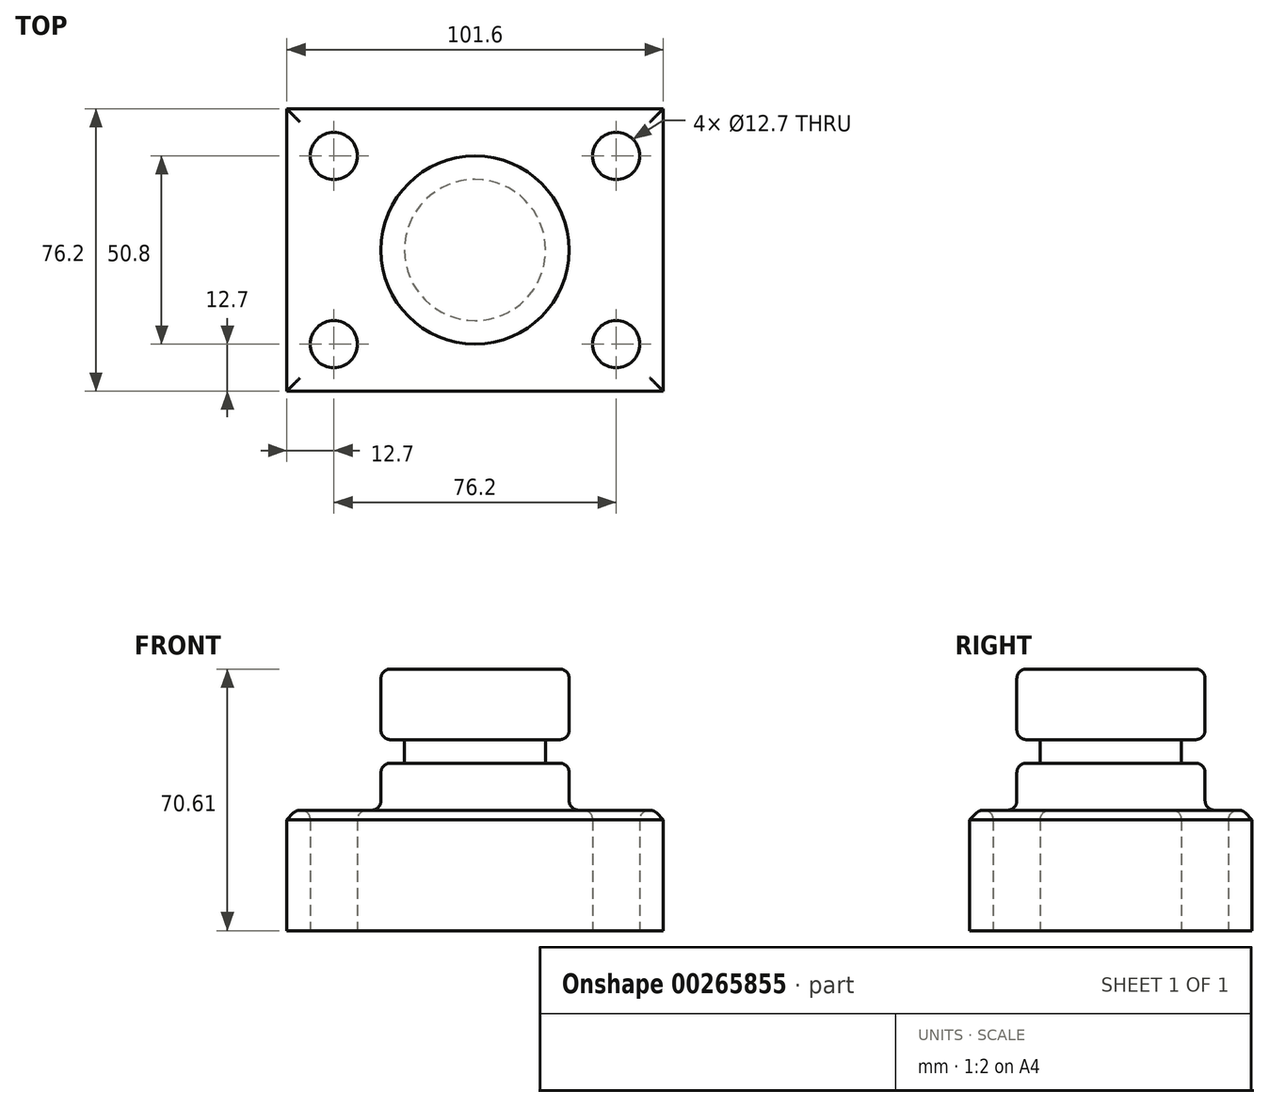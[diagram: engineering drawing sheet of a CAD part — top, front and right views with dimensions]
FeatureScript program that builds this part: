
annotation { "Feature Type Name" : "Feature", "Feature Type Description" : "" }
export const myFeature = defineFeature(function(context is Context, id is Id, definition is map)
    precondition{}
    {
        {
            var Q0;
            Q0=qCreatedBy(makeId("Top.planeOp"),FACE);
            var sketch = newSketch(context, id + "F0", { "sketchPlane" : qUnion([Q0])});
            skLineSegment(sketch, "E0.bottom", {"start": v(50.8, 38.1) * mm, "end": v(-50.8, 38.1) * mm});
            skLineSegment(sketch, "E0.top", {"start": v(50.8, -38.1) * mm, "end": v(-50.8, -38.1) * mm});
            skLineSegment(sketch, "E0.left", {"start": v(50.8, 38.1) * mm, "end": v(50.8, -38.1) * mm});
            skLineSegment(sketch, "E0.right", {"start": v(-50.8, 38.1) * mm, "end": v(-50.8, -38.1) * mm});
            skPoint(sketch, "E0.middle", {"position": v(0, 0) * mm});
            skSolve(sketch);
        }
        {
            var Q0;
            Q0 = qSketchRegion(id + "F0", true);
            extrude(context, id + "F1", {"entities" : qUnion([Q0]), "depth" : 32.5 * mm});
        }
        {
            var Q0;
            Q0=qCreatedBy(makeId("Top.planeOp"),FACE);
            var sketch = newSketch(context, id + "F2", { "sketchPlane" : qUnion([Q0])});
            skCircle(sketch, "E1", {"center": v(-38.1, -25.4) * mm, "radius": 6.35 * mm});
            skCircle(sketch, "E2", {"center": v(38.1, -25.4) * mm, "radius": 6.35 * mm});
            skCircle(sketch, "E3", {"center": v(-38.1, 25.4) * mm, "radius": 6.35 * mm});
            skCircle(sketch, "E4", {"center": v(38.1, 25.4) * mm, "radius": 6.35 * mm});
            skSolve(sketch);
        }
        {
            var Q0;
            Q0=makeQuery(id+"F2.imprint","IMPRINT",FACE,{"disambiguationData":[TD([[makeQuery(id+"F2.imprint","IMPRINT",EDGE,{"derivedFrom":sQuery(id+"F2.wireOp",EDGE,"E1")}),1.0]])]});
            extrude(context, id + "F3", {"entities" : qUnion([Q0]), "operationType" : NewBodyOperationType.REMOVE, "depth" : 32.77 * mm});
        }
        {
            var Q0;
            Q0 = qSketchRegion(id + "F2", true);
            extrude(context, id + "F4", {"entities" : qUnion([Q0]), "operationType" : NewBodyOperationType.REMOVE, "depth" : 32.77 * mm});
        }
        {
            var Q0;
            Q0=qCreatedBy(makeId("Front.planeOp"),FACE);
            var sketch = newSketch(context, id + "F5", { "sketchPlane" : qUnion([Q0])});
            skLineSegment(sketch, "E5.bottom", {"start": v(0, 70.61) * mm, "end": v(-25.4, 70.61) * mm});
            skLineSegment(sketch, "E5.top", {"start": v(0, 32.51) * mm, "end": v(-25.4, 32.51) * mm});
            skLineSegment(sketch, "E5.left", {"start": v(0, 70.61) * mm, "end": v(0, 32.51) * mm});
            skLineSegment(sketch, "E5.right", {"start": v(-25.4, 70.61) * mm, "end": v(-25.4, 32.51) * mm});
            skSolve(sketch);
        }
        {
            var Q0;
            Q0 = qSketchRegion(id + "F5", true);
            var Q1;
            Q1=sQuery(id+"F5.wireOp",EDGE,"E5.left");
            revolve(context, id + "F6", {"operationType" : NewBodyOperationType.ADD, "entities" : qUnion([Q0]), "axis" : qUnion([Q1]), "revolveType" : RevolveType.FULL});
        }
        {
            var Q0;
            Q0=qCreatedBy(makeId("Right.planeOp"),FACE);
            var sketch = newSketch(context, id + "F7", { "sketchPlane" : qUnion([Q0])});
            skLineSegment(sketch, "E6.bottom", {"start": v(-19.05, 51.56) * mm, "end": v(-34.38, 51.56) * mm});
            skLineSegment(sketch, "E6.top", {"start": v(-19.05, 45.21) * mm, "end": v(-34.38, 45.21) * mm});
            skLineSegment(sketch, "E6.left", {"start": v(-19.05, 51.56) * mm, "end": v(-19.05, 45.21) * mm});
            skLineSegment(sketch, "E6.right", {"start": v(-34.38, 51.56) * mm, "end": v(-34.38, 45.21) * mm});
            skSolve(sketch);
        }
        {
            var Q0;
            Q0=makeQuery(id+"F7.imprint","IMPRINT",FACE,{"disambiguationData":[TD([[makeQuery(id+"F7.imprint","IMPRINT",EDGE,{"derivedFrom":sQuery(id+"F7.wireOp",EDGE,"E6.bottom")}),1.0]])]});
            var Q1;
            Q1=makeQuery(id+"F6.opRevolve","SWEPT_FACE",FACE,{"disambiguationData":[OSD([sQuery(id+"F5.wireOp",EDGE,"E5.right")])]});
            revolve(context, id + "F8", {"operationType" : NewBodyOperationType.REMOVE, "entities" : qUnion([Q0]), "axis" : qUnion([Q1]), "revolveType" : RevolveType.FULL, "oppositeDirection" : true});
        }
        {
            var Q0;
            Q0=makeQuery(id+"F1.opExtrude","CAP_EDGE",EDGE,{"disambiguationData":[OSD([sQuery(id+"F0.wireOp",EDGE,"E0.left")])],"isStart":false});
            var Q1;
            Q1=makeQuery(id+"F1.opExtrude","CAP_EDGE",EDGE,{"disambiguationData":[OSD([sQuery(id+"F0.wireOp",EDGE,"E0.bottom")])],"isStart":false});
            var Q2;
            Q2=makeQuery(id+"F1.opExtrude","CAP_EDGE",EDGE,{"disambiguationData":[OSD([sQuery(id+"F0.wireOp",EDGE,"E0.right")])],"isStart":false});
            var Q3;
            Q3=makeQuery(id+"F1.opExtrude","CAP_EDGE",EDGE,{"disambiguationData":[OSD([sQuery(id+"F0.wireOp",EDGE,"E0.top")])],"isStart":false});
            chamfer(context, id + "F9", {"entities" : qUnion([Q0, Q1, Q2, Q3]), "width" : 2.54 * mm, "tangentPropagation" : true});
        }
        {
            var Q0;
            Q0=makeQuery(id+"F6.opRevolve","SWEPT_EDGE",EDGE,{"disambiguationData":[OSD([sQuery(id+"F5.wireOp",EDGE,"E5.bottom"),sQuery(id+"F5.wireOp",EDGE,"E5.right")])]});
            var Q1;
            Q1=makeQuery(id+"F8.boolean.opBoolean","INTERSECT",EDGE,{"derivedFrom":[makeQuery(id+"F6.opRevolve","SWEPT_FACE",FACE,{"disambiguationData":[OSD([sQuery(id+"F5.wireOp",EDGE,"E5.right")])]}),makeQuery(id+"F8.opRevolve","SWEPT_FACE",FACE,{"disambiguationData":[OSD([sQuery(id+"F7.wireOp",EDGE,"E6.top")])]})]});
            var Q2;
            Q2=makeQuery(id+"F8.boolean.opBoolean","INTERSECT",EDGE,{"derivedFrom":[makeQuery(id+"F6.opRevolve","SWEPT_FACE",FACE,{"disambiguationData":[OSD([sQuery(id+"F5.wireOp",EDGE,"E5.right")])]}),makeQuery(id+"F8.opRevolve","SWEPT_FACE",FACE,{"disambiguationData":[OSD([sQuery(id+"F7.wireOp",EDGE,"E6.bottom")])]})]});
            var Q3;
            Q3=makeQuery(id+"F4.boolean.opBoolean","INTERSECT",EDGE,{"derivedFrom":[makeQuery(id+"F1.opExtrude","CAP_FACE",FACE,{"disambiguationData":[OSD([sQuery(id+"F0.wireOp",EDGE,"E0.bottom"),sQuery(id+"F0.wireOp",EDGE,"E0.top"),sQuery(id+"F0.wireOp",EDGE,"E0.left"),sQuery(id+"F0.wireOp",EDGE,"E0.right")])],"isStart":false}),makeQuery(id+"F4.opExtrude","SWEPT_FACE",FACE,{"disambiguationData":[OSD([sQuery(id+"F2.wireOp",EDGE,"E4")])]})]});
            var Q4;
            Q4=makeQuery(id+"F1.opExtrude","CAP_FACE",FACE,{"disambiguationData":[OSD([sQuery(id+"F0.wireOp",EDGE,"E0.bottom"),sQuery(id+"F0.wireOp",EDGE,"E0.top"),sQuery(id+"F0.wireOp",EDGE,"E0.left"),sQuery(id+"F0.wireOp",EDGE,"E0.right")])],"isStart":false});
            var Q5;
            Q5=makeQuery(id+"F4.boolean.opBoolean","INTERSECT",EDGE,{"derivedFrom":[makeQuery(id+"F1.opExtrude","CAP_FACE",FACE,{"disambiguationData":[OSD([sQuery(id+"F0.wireOp",EDGE,"E0.bottom"),sQuery(id+"F0.wireOp",EDGE,"E0.top"),sQuery(id+"F0.wireOp",EDGE,"E0.left"),sQuery(id+"F0.wireOp",EDGE,"E0.right")])],"isStart":false}),makeQuery(id+"F4.opExtrude","SWEPT_FACE",FACE,{"disambiguationData":[OSD([sQuery(id+"F2.wireOp",EDGE,"E2")])]})]});
            var Q6;
            Q6=makeQuery(id+"F3.boolean.opBoolean","INTERSECT",EDGE,{"derivedFrom":[makeQuery(id+"F1.opExtrude","CAP_FACE",FACE,{"disambiguationData":[OSD([sQuery(id+"F0.wireOp",EDGE,"E0.bottom"),sQuery(id+"F0.wireOp",EDGE,"E0.top"),sQuery(id+"F0.wireOp",EDGE,"E0.left"),sQuery(id+"F0.wireOp",EDGE,"E0.right")])],"isStart":false}),makeQuery(id+"F3.opExtrude","SWEPT_FACE",FACE,{"disambiguationData":[OSD([sQuery(id+"F2.wireOp",EDGE,"E1")])]})]});
            var Q7;
            Q7=makeQuery(id+"F4.boolean.opBoolean","INTERSECT",EDGE,{"derivedFrom":[makeQuery(id+"F1.opExtrude","CAP_FACE",FACE,{"disambiguationData":[OSD([sQuery(id+"F0.wireOp",EDGE,"E0.bottom"),sQuery(id+"F0.wireOp",EDGE,"E0.top"),sQuery(id+"F0.wireOp",EDGE,"E0.left"),sQuery(id+"F0.wireOp",EDGE,"E0.right")])],"isStart":false}),makeQuery(id+"F4.opExtrude","SWEPT_FACE",FACE,{"disambiguationData":[OSD([sQuery(id+"F2.wireOp",EDGE,"E3")])]})]});
            fillet(context, id + "F10", {"entities" : qUnion([Q0, Q1, Q2, Q3, Q4, Q5, Q6, Q7]), "radius" : 2.54 * mm, "tangentPropagation" : true, "allowEdgeOverflow" : false});
        }
    });
